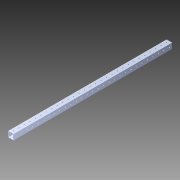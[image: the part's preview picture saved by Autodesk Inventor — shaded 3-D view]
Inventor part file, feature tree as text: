
AUTODESK INVENTOR PART (.ipt)
format: ipt  version: 2014 (Build 180170000, 170)  size: 1,271,296 bytes
history: native  units: in
note: dims shown in document units (in); Inventor stores cm internally (conversion verified against a paired STEP export)
features: pattern_circular x1, other x1, extrude x1, imported_body x1, sketch x1
ambient origin geometry x8: Origin, YZ Plane, XZ Plane, XY Plane, X Axis, Y Axis, Z Axis, Center Point
bodies: Body1 (feature_tree)
feature tree (5):
  pattern_circular  "CirPattern2"
  other  "1x1 tube1"
  extrude  "Extrusion1"  [1 undecoded]
  imported_body  "Base1"
  sketch  "Sketch1"  dims[d0=30.0in d1=0.0in]
note: 1 required parameter value undecoded (feature->parameter linkage not recoverable at this tier; creation-order binding heuristic only, values carry confidence <= 0.55)
